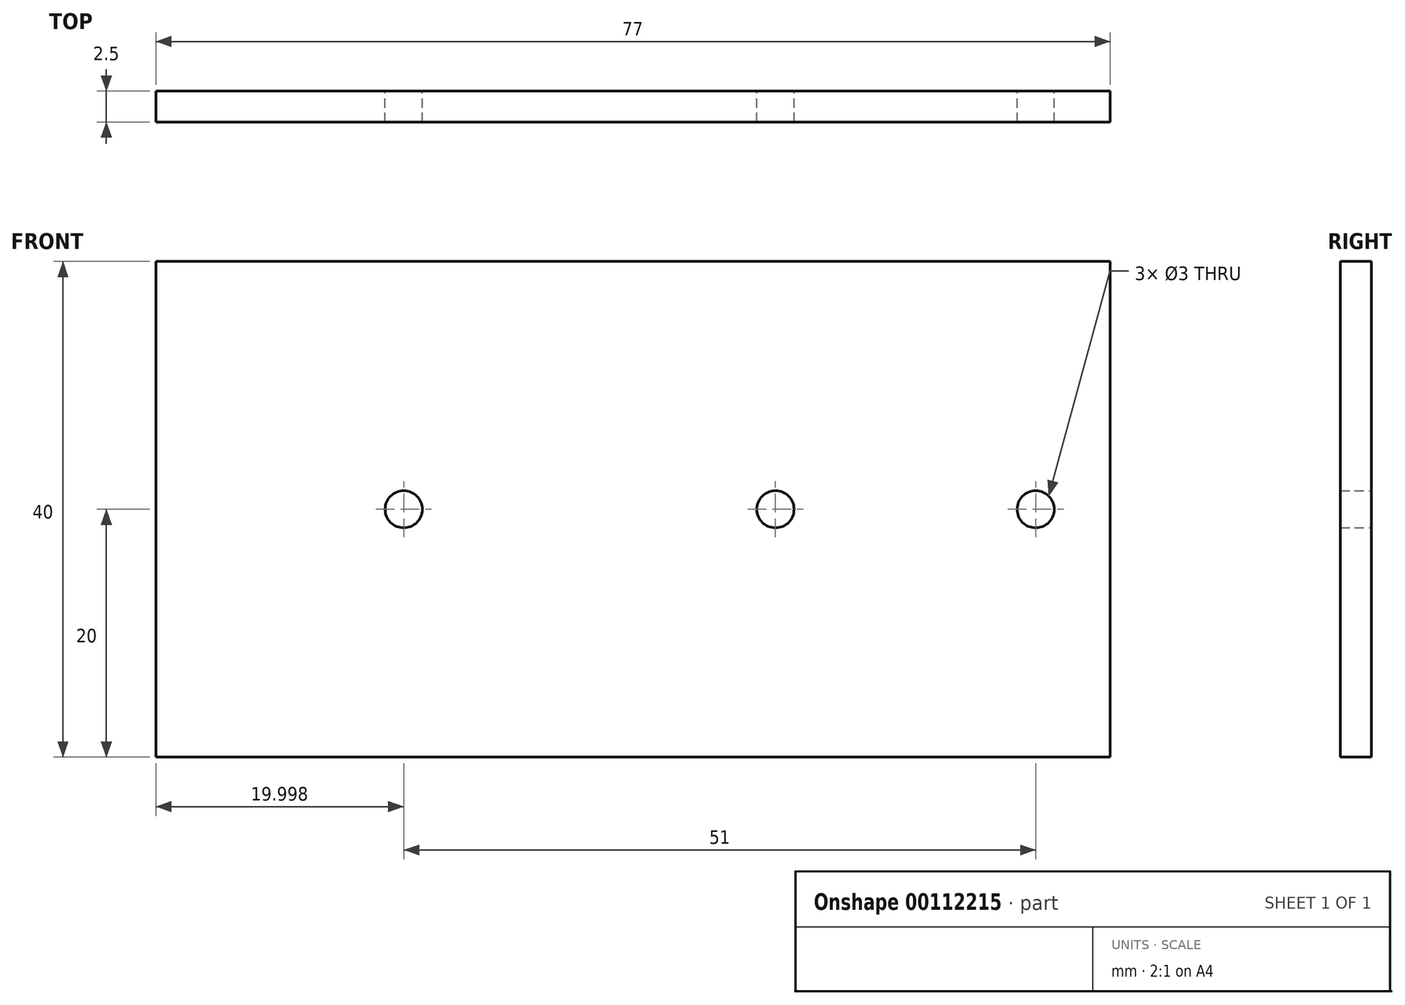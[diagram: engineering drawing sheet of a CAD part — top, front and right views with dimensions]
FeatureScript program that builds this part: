
annotation { "Feature Type Name" : "Feature", "Feature Type Description" : "" }
export const myFeature = defineFeature(function(context is Context, id is Id, definition is map)
    precondition{}
    {
        {
            var Q0;
            Q0=qCreatedBy(makeId("Front.planeOp"),FACE);
            var sketch = newSketch(context, id + "F0", { "sketchPlane" : qUnion([Q0])});
            skLineSegment(sketch, "E0.bottom", {"start": v(-79.41, 0) * mm, "end": v(-2.41, 0) * mm});
            skLineSegment(sketch, "E0.top", {"start": v(-79.41, 40) * mm, "end": v(-2.41, 40) * mm});
            skLineSegment(sketch, "E0.left", {"start": v(-79.41, 0) * mm, "end": v(-79.41, 40) * mm});
            skLineSegment(sketch, "E0.right", {"start": v(-2.41, 0) * mm, "end": v(-2.41, 40) * mm});
            skCircle(sketch, "E1", {"center": v(-59.41, 20) * mm, "radius": 1.5 * mm});
            skPoint(sketch, "E1.centerSnap0", {"position": v(-79.41, 20) * mm});
            skCircle(sketch, "E2", {"center": v(-29.41, 20) * mm, "radius": 1.5 * mm});
            skCircle(sketch, "E3", {"center": v(-8.41, 20) * mm, "radius": 1.5 * mm});
            skSolve(sketch);
        }
        {
            var Q0;
            Q0=makeQuery(id+"F0.imprint","IMPRINT",FACE,{"disambiguationData":[TD([[makeQuery(id+"F0.imprint","IMPRINT",EDGE,{"derivedFrom":sQuery(id+"F0.wireOp",EDGE,"E0.bottom")}),1.0]])]});
            extrude(context, id + "F1", {"entities" : qUnion([Q0]), "depth" : 2.5 * mm});
        }
    });
